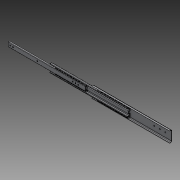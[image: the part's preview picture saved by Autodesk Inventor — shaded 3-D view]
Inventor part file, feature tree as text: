
AUTODESK INVENTOR PART (.ipt)
format: ipt  version: 2014 SP1 (Build 180222100, 222)  size: 416,256 bytes
history: native  units: in
note: dims shown in document units (in); Inventor stores cm internally (conversion verified against a paired STEP export)
features: imported_body x5, other x3, mirror x2, extrude x1
ambient origin geometry x8: Origin, YZ Plane, XZ Plane, XY Plane, X Axis, Y Axis, Z Axis, Center Point
bodies: Body1 (feature_tree), Body2 (feature_tree), Body3 (feature_tree), Body4 (feature_tree), Body5 (feature_tree)
feature tree (11):
  extrude  "Extrude3"  [1 undecoded]
  other  "63835A4201"
  other  "Cut-Extrude1"
  other  "Cut-Extrude2"
  mirror  "Mirror2"
  mirror  "Mirror3"
  imported_body  "Base1"
  imported_body  "Base2"
  imported_body  "Base3"
  imported_body  "Base4"
  imported_body  "Base5"
note: 1 required parameter value undecoded (feature->parameter linkage not recoverable at this tier; creation-order binding heuristic only, values carry confidence <= 0.55)
